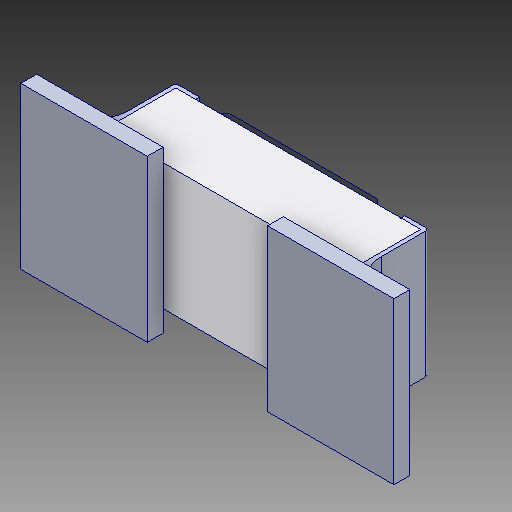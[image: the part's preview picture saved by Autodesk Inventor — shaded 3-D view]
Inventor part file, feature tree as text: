
AUTODESK INVENTOR PART (.ipt)
format: ipt  version: 2018 (Build 220112000, 112)  size: 230,400 bytes
history: native  units: mm
features: other x2, fillet x2
ambient origin geometry x8: Origin, YZ Plane, XZ Plane, XY Plane, X Axis, Y Axis, Z Axis, Center Point
bodies: Volumenkörper1 (feature_tree), Volumenkörper2 (feature_tree), Volumenkörper3 (feature_tree), Volumenkörper4 (feature_tree)
feature tree (4):
  other  "Boss-Extrude1"
  other  "Boss-Extrude4"
  fillet  "Fillet6"  [1 undecoded]
  fillet  "Fillet5"  [1 undecoded]
note: 2 required parameter values undecoded (feature->parameter linkage not recoverable at this tier; creation-order binding heuristic only, values carry confidence <= 0.55)
